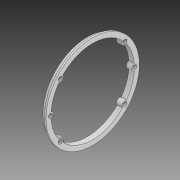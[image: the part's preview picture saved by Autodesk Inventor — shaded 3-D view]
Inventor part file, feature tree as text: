
AUTODESK INVENTOR PART (.ipt)
format: ipt  version: 2020 (Build 240168000, 168)  size: 171,008 bytes
history: native  units: mm
features: sketch x3, extrude x3, revolve x1
ambient origin geometry x8: Origin, YZ Plane, XZ Plane, XY Plane, X Axis, Y Axis, Z Axis, Center Point
bodies: Solid1 (feature_tree)
feature tree (7):
  revolve  "Revolution1"  Angle=90.0deg
  sketch  "Sketch2"  dims[d9=6.981317mm d10=6.981317mm d11=7.0mm d12=9.0mm d13=3.5mm d14=10.0mm d15=0.0mm]
  extrude  "Extrusion1"  Depth=10.0mm TaperAngle=0.0deg
  extrude  "Extrusion2"  Depth=3.0mm
  extrude  "Extrusion3"  Depth=3.0mm TaperAngle=0.0deg
  sketch  "Sketch1"  dims[d0=63.4mm d1=4.0mm d2=2.5mm d3=3.0mm d4=5.0mm d8=90.0deg]
  sketch  "Sketch3"  dims[d16=0.0mm d17=0.0mm d18=6.0mm d19=3.0mm d20=0.0mm]
